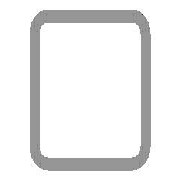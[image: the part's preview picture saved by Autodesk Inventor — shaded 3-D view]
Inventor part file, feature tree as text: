
AUTODESK INVENTOR PART (.ipt)
format: ipt  version: 2025.1 (Build 291241020, 241B)  size: 134,656 bytes
history: native  units: mm (DEFAULTED — no unit token found)
features: other x4, sketch x1, plane x1
ambient origin geometry x8: Origin, YZ Plane, XZ Plane, XY Plane, X Axis, Y Axis, Z Axis, Center Point
bodies: Solid1 (feature_tree), Body (feature_tree)
feature tree (6):
  parser-record x1  (decoder bookkeeping rows leaked as tree rows — omitted from the tree; the rows remain in map.json)
  other  "Driven Length"
  other  "Start Plane"
  other  "End Plane"
  sketch  "Sketch3"  dims[d3=790.0mm d4=0.0mm d7=4.0mm d9=40.0mm d11=40.0mm d12=2.0mm d13=100.0mm d14=890.0mm d15=20.0mm d16=20.0mm d17=90.0deg d18=790.0mm]
  plane  "Work Plane3"
